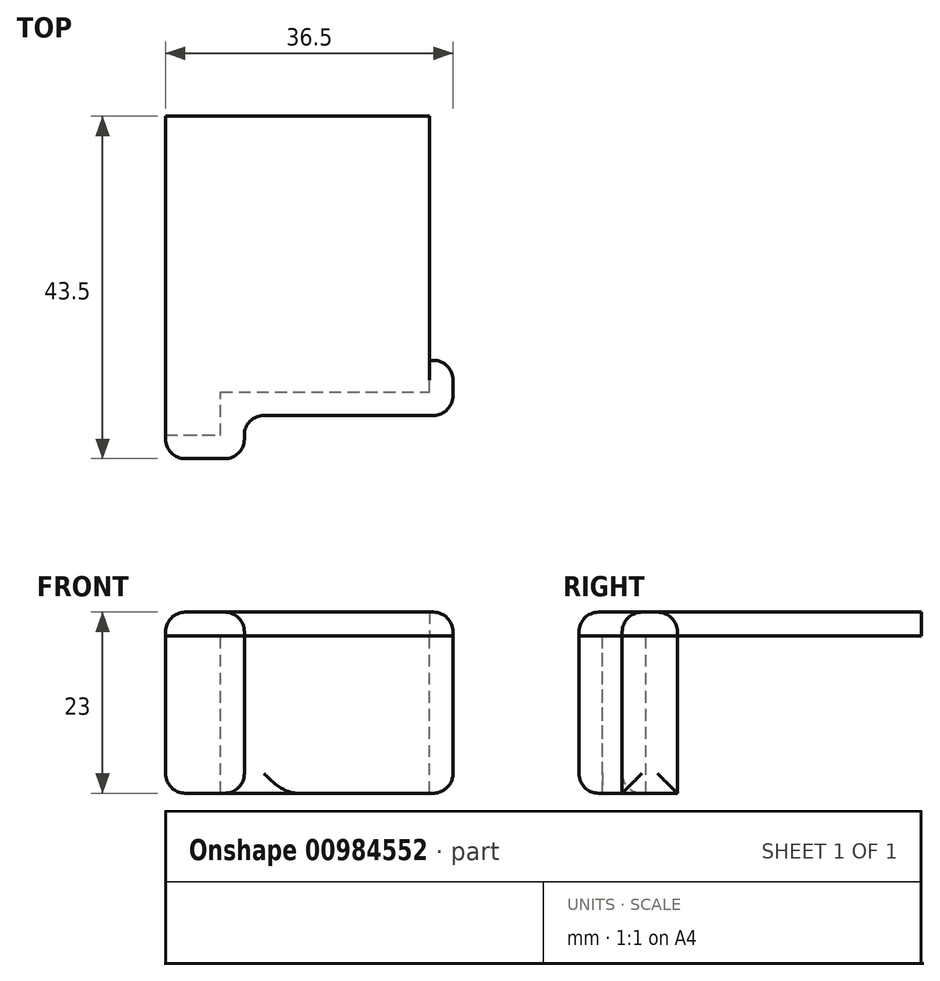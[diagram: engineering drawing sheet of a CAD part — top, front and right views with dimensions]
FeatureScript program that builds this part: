
annotation { "Feature Type Name" : "Feature", "Feature Type Description" : "" }
export const myFeature = defineFeature(function(context is Context, id is Id, definition is map)
    precondition{}
    {
        {
            var Q0;
            Q0=qCreatedBy(makeId("Top.planeOp"),FACE);
            var sketch = newSketch(context, id + "F0", { "sketchPlane" : qUnion([Q0])});
            skLineSegment(sketch, "E0", {"start": v(-14.47, -8.7) * mm, "end": v(-7.47, -8.7) * mm});
            skLineSegment(sketch, "E1", {"start": v(-7.47, -8.7) * mm, "end": v(-7.47, -3.2) * mm});
            skLineSegment(sketch, "E2", {"start": v(-7.47, -3.2) * mm, "end": v(19.03, -3.2) * mm});
            skLineSegment(sketch, "E3", {"start": v(19.03, -3.2) * mm, "end": v(19.03, 31.8) * mm});
            skLineSegment(sketch, "E4", {"start": v(19.03, 31.8) * mm, "end": v(-14.47, 31.8) * mm});
            skLineSegment(sketch, "E5", {"start": v(-14.47, 31.8) * mm, "end": v(-14.47, -8.7) * mm});
            skLineSegment(sketch, "E6", {"start": v(-17.47, 31.8) * mm, "end": v(-17.47, -8.7) * mm});
            skLineSegment(sketch, "E7", {"start": v(-17.47, -8.7) * mm, "end": v(-17.47, -11.7) * mm});
            skLineSegment(sketch, "E8", {"start": v(-17.47, -11.7) * mm, "end": v(-7.47, -11.7) * mm});
            skLineSegment(sketch, "E9", {"start": v(-7.47, -11.7) * mm, "end": v(-4.47, -11.7) * mm});
            skLineSegment(sketch, "E10", {"start": v(-17.47, 31.8) * mm, "end": v(-17.47, 34.8) * mm});
            skLineSegment(sketch, "E11", {"start": v(-17.47, 34.8) * mm, "end": v(19.03, 34.8) * mm});
            skLineSegment(sketch, "E12", {"start": v(19.03, 34.8) * mm, "end": v(22.03, 34.8) * mm});
            skLineSegment(sketch, "E13", {"start": v(22.03, 34.8) * mm, "end": v(22.03, -3.2) * mm});
            skLineSegment(sketch, "E14", {"start": v(22.03, -3.2) * mm, "end": v(22.03, -6.2) * mm});
            skLineSegment(sketch, "E15", {"start": v(22.03, -6.2) * mm, "end": v(-4.47, -6.2) * mm});
            skLineSegment(sketch, "E16", {"start": v(-4.47, -6.2) * mm, "end": v(-4.47, -11.7) * mm});
            skLineSegment(sketch, "E17", {"start": v(19.03, -3.2) * mm, "end": v(19.03, -6.2) * mm});
            skLineSegment(sketch, "E18", {"start": v(19.03, -6.2) * mm, "end": v(19.03, 34.8) * mm});
            skLineSegment(sketch, "E19", {"start": v(-4.47, -6.2) * mm, "end": v(-4.47, -3.2) * mm});
            skLineSegment(sketch, "E20", {"start": v(-14.47, -8.7) * mm, "end": v(-14.47, -11.7) * mm});
            skLineSegment(sketch, "E21", {"start": v(-14.47, -8.7) * mm, "end": v(-17.47, -8.7) * mm});
            skLineSegment(sketch, "E22", {"start": v(19.03, 31.8) * mm, "end": v(22.03, 31.8) * mm});
            skLineSegment(sketch, "E23", {"start": v(-14.47, 31.8) * mm, "end": v(-17.47, 31.8) * mm});
            skLineSegment(sketch, "E24", {"start": v(22.03, -6.2) * mm, "end": v(22.03, 0.8) * mm});
            skLineSegment(sketch, "E25", {"start": v(22.03, 0.8) * mm, "end": v(19.03, 0.8) * mm});
            skSolve(sketch);
        }
        {
            var Q0;
            Q0=makeQuery(id+"F0.imprint","IMPRINT",FACE,{"disambiguationData":[TD([[makeQuery(id+"F0.imprint","IMPRINT",EDGE,{"derivedFrom":sQuery(id+"F0.wireOp",EDGE,"E0")}),1.0]])]});
            var Q1;
            Q1=makeQuery(id+"F0.imprint","IMPRINT",FACE,{"disambiguationData":[TD([[makeQuery(id+"F0.imprint","IMPRINT",EDGE,{"derivedFrom":sQuery(id+"F0.wireOp",EDGE,"E0")}),-1.0]])]});
            var Q2;
            {var subQ3=sQuery(id+"F0.wireOp",EDGE,"E19");Q2=makeQuery(id+"F0.imprint","IMPRINT",FACE,{"disambiguationData":[TD([[makeQuery(id+"F0.imprint","IMPRINT",EDGE,{"derivedFrom":subQ3}),-1.0]])]});}
            var Q3;
            {var subQ1=sQuery(id+"F0.wireOp",EDGE,"E14");Q3=makeQuery(id+"F0.imprint","IMPRINT",FACE,{"disambiguationData":[TD([[makeQuery(id+"F0.imprint","IMPRINT",EDGE,{"derivedFrom":subQ1}),-1.0]])]});}
            var Q4;
            {var subQ0=sQuery(id+"F0.wireOp",EDGE,"E24");Q4=makeQuery(id+"F0.imprint","IMPRINT",FACE,{"disambiguationData":[TD([[makeQuery(id+"F0.imprint","IMPRINT",EDGE,{"derivedFrom":subQ0}),1.0]])]});}
            extrude(context, id + "F1", {"entities" : qUnion([Q0, Q1, Q2, Q3, Q4]), "depth" : 3 * mm, "offsetDistance" : 25 * mm});
        }
        {
            var Q0;
            Q0=makeQuery(id+"F0.imprint","IMPRINT",FACE,{"disambiguationData":[TD([[makeQuery(id+"F0.imprint","IMPRINT",EDGE,{"derivedFrom":sQuery(id+"F0.wireOp",EDGE,"E0")}),-1.0]])]});
            var Q1;
            {var subQ3=sQuery(id+"F0.wireOp",EDGE,"E19");Q1=makeQuery(id+"F0.imprint","IMPRINT",FACE,{"disambiguationData":[TD([[makeQuery(id+"F0.imprint","IMPRINT",EDGE,{"derivedFrom":subQ3}),-1.0]])]});}
            var Q2;
            {var subQ1=sQuery(id+"F0.wireOp",EDGE,"E14");Q2=makeQuery(id+"F0.imprint","IMPRINT",FACE,{"disambiguationData":[TD([[makeQuery(id+"F0.imprint","IMPRINT",EDGE,{"derivedFrom":subQ1}),-1.0]])]});}
            var Q3;
            {var subQ0=sQuery(id+"F0.wireOp",EDGE,"E24");Q3=makeQuery(id+"F0.imprint","IMPRINT",FACE,{"disambiguationData":[TD([[makeQuery(id+"F0.imprint","IMPRINT",EDGE,{"derivedFrom":subQ0}),1.0]])]});}
            extrude(context, id + "F2", {"entities" : qUnion([Q0, Q1, Q2, Q3]), "oppositeDirection" : true, "depth" : 20 * mm, "offsetDistance" : 25 * mm});
        }
        {
            var Q0;
            Q0=makeQuery(id+"F1.opExtrude","CAP_EDGE",EDGE,{"disambiguationData":[OSD([sQuery(id+"F0.wireOp",EDGE,"E8"),sQuery(id+"F0.wireOp",EDGE,"E9")])],"isStart":false});
            var Q1;
            Q1=makeQuery(id+"F1.opExtrude","CAP_EDGE",EDGE,{"disambiguationData":[OSD([sQuery(id+"F0.wireOp",EDGE,"E16")])],"isStart":false});
            var Q2;
            Q2=makeQuery(id+"F1.opExtrude","CAP_EDGE",EDGE,{"disambiguationData":[OSD([sQuery(id+"F0.wireOp",EDGE,"E15")])],"isStart":false});
            var Q3;
            Q3=makeQuery(id+"F1.opExtrude","CAP_EDGE",EDGE,{"disambiguationData":[OSD([sQuery(id+"F0.wireOp",EDGE,"E13"),sQuery(id+"F0.wireOp",EDGE,"E14")])],"isStart":false});
            var Q4;
            Q4=makeQuery(id+"F2.opExtrude","SWEPT_EDGE",EDGE,{"disambiguationData":[OSD([sQuery(id+"F0.wireOp",EDGE,"E14"),sQuery(id+"F0.wireOp",EDGE,"E15")])]});
            var Q5;
            Q5=makeQuery(id+"F1.opExtrude","SWEPT_EDGE",EDGE,{"disambiguationData":[OSD([sQuery(id+"F0.wireOp",EDGE,"E14"),sQuery(id+"F0.wireOp",EDGE,"E15")])]});
            var Q6;
            Q6=makeQuery(id+"F1.opExtrude","SWEPT_EDGE",EDGE,{"disambiguationData":[OSD([sQuery(id+"F0.wireOp",EDGE,"E9"),sQuery(id+"F0.wireOp",EDGE,"E16")])]});
            var Q7;
            Q7=makeQuery(id+"F2.opExtrude","SWEPT_EDGE",EDGE,{"disambiguationData":[OSD([sQuery(id+"F0.wireOp",EDGE,"E9"),sQuery(id+"F0.wireOp",EDGE,"E16")])]});
            var Q8;
            Q8=makeQuery(id+"F2.opExtrude","SWEPT_EDGE",EDGE,{"disambiguationData":[OSD([sQuery(id+"F0.wireOp",EDGE,"E15"),sQuery(id+"F0.wireOp",EDGE,"E16"),sQuery(id+"F0.wireOp",EDGE,"E19")])]});
            var Q9;
            Q9=makeQuery(id+"F1.opExtrude","SWEPT_EDGE",EDGE,{"disambiguationData":[OSD([sQuery(id+"F0.wireOp",EDGE,"E15"),sQuery(id+"F0.wireOp",EDGE,"E16"),sQuery(id+"F0.wireOp",EDGE,"E19")])]});
            var Q10;
            Q10=makeQuery(id+"F2.opExtrude","SWEPT_EDGE",EDGE,{"disambiguationData":[OSD([sQuery(id+"F0.wireOp",EDGE,"E8"),sQuery(id+"F0.wireOp",EDGE,"E20")])]});
            var Q11;
            Q11=makeQuery(id+"F1.opExtrude","SWEPT_EDGE",EDGE,{"disambiguationData":[OSD([sQuery(id+"F0.wireOp",EDGE,"E8"),sQuery(id+"F0.wireOp",EDGE,"E20")])]});
            var Q12;
            Q12=makeQuery(id+"F1.opExtrude","CAP_EDGE",EDGE,{"disambiguationData":[OSD([sQuery(id+"F0.wireOp",EDGE,"E5"),sQuery(id+"F0.wireOp",EDGE,"E20")])],"isStart":false});
            var Q13;
            Q13=makeQuery(id+"F2.opExtrude","CAP_EDGE",EDGE,{"disambiguationData":[OSD([sQuery(id+"F0.wireOp",EDGE,"E8"),sQuery(id+"F0.wireOp",EDGE,"E9")])],"isStart":false});
            var Q14;
            Q14=makeQuery(id+"F2.opExtrude","CAP_EDGE",EDGE,{"disambiguationData":[OSD([sQuery(id+"F0.wireOp",EDGE,"E16")])],"isStart":false});
            var Q15;
            Q15=makeQuery(id+"F2.opExtrude","CAP_EDGE",EDGE,{"disambiguationData":[OSD([sQuery(id+"F0.wireOp",EDGE,"E13"),sQuery(id+"F0.wireOp",EDGE,"E14")])],"isStart":false});
            var Q16;
            Q16=makeQuery(id+"F2.opExtrude","CAP_EDGE",EDGE,{"disambiguationData":[OSD([sQuery(id+"F0.wireOp",EDGE,"E20")])],"isStart":false});
            var Q17;
            Q17=makeQuery(id+"F1.opExtrude","CAP_EDGE",EDGE,{"disambiguationData":[OSD([sQuery(id+"F0.wireOp",EDGE,"E24")])],"isStart":false});
            var Q18;
            Q18=makeQuery(id+"F2.opExtrude","CAP_EDGE",EDGE,{"disambiguationData":[OSD([sQuery(id+"F0.wireOp",EDGE,"E24")])],"isStart":false});
            var Q19;
            Q19=makeQuery(id+"F1.opExtrude","CAP_EDGE",EDGE,{"disambiguationData":[OSD([sQuery(id+"F0.wireOp",EDGE,"E25")])],"isStart":false});
            var Q20;
            Q20=makeQuery(id+"F2.opExtrude","SWEPT_EDGE",EDGE,{"disambiguationData":[OSD([sQuery(id+"F0.wireOp",EDGE,"E13"),sQuery(id+"F0.wireOp",EDGE,"E24"),sQuery(id+"F0.wireOp",EDGE,"E25")])]});
            var Q21;
            Q21=makeQuery(id+"F1.opExtrude","SWEPT_EDGE",EDGE,{"disambiguationData":[OSD([sQuery(id+"F0.wireOp",EDGE,"E13"),sQuery(id+"F0.wireOp",EDGE,"E24"),sQuery(id+"F0.wireOp",EDGE,"E25")])]});
            var Q22;
            Q22=makeQuery(id+"F1.opExtrude","CAP_EDGE",EDGE,{"disambiguationData":[OSD([sQuery(id+"F0.wireOp",EDGE,"E18")])],"isStart":false});
            fillet(context, id + "F3", {"entities" : qUnion([Q0, Q1, Q2, Q3, Q4, Q5, Q6, Q7, Q8, Q9, Q10, Q11, Q12, Q13, Q14, Q15, Q16, Q17, Q18, Q19, Q20, Q21, Q22]), "radius" : 2.5 * mm, "tangentPropagation" : true, "allowEdgeOverflow" : false});
        }
    });
